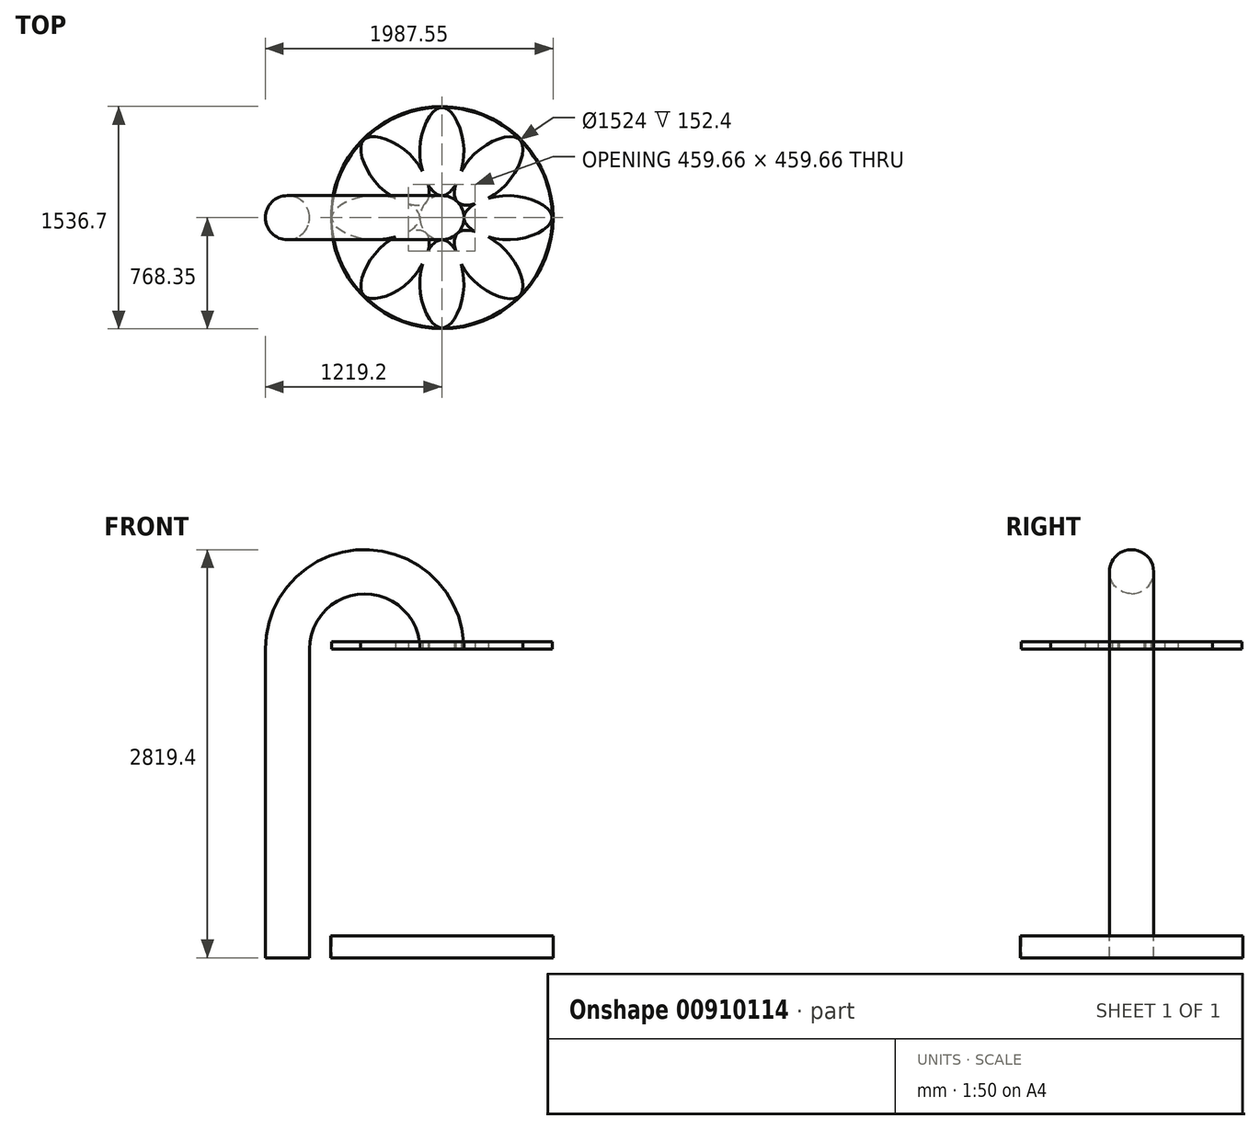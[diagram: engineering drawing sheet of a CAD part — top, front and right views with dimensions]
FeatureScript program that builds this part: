
annotation { "Feature Type Name" : "Feature", "Feature Type Description" : "" }
export const myFeature = defineFeature(function(context is Context, id is Id, definition is map)
    precondition{}
    {
        {
            var Q0;
            Q0=qCreatedBy(makeId("Top.planeOp"),FACE);
            var sketch = newSketch(context, id + "F0", { "sketchPlane" : qUnion([Q0])});
            skCircle(sketch, "E0", {"center": v(0, 0) * mm, "radius": 762 * mm});
            skCircle(sketch, "E1", {"center": v(0, 0) * mm, "radius": 768.35 * mm});
            skSolve(sketch);
        }
        {
            var Q0;
            Q0=qCreatedBy(makeId("Front.planeOp"),FACE);
            var sketch = newSketch(context, id + "F1", { "sketchPlane" : qUnion([Q0])});
            skLineSegment(sketch, "E2", {"start": v(-1066.8, 0) * mm, "end": v(-1066.8, 2133.6) * mm});
            skArc(sketch, "E3", {"start": v(0, 2133.6) * mm, "mid": v(-533.4, 2667) * mm, "end": v(-1066.8, 2133.6) * mm});
            skSolve(sketch);
        }
        {
            var Q0;
            Q0 = qSketchRegion(id + "F0", true);
            extrude(context, id + "F2", {"entities" : qUnion([Q0]), "depth" : 152.4 * mm, "offsetDistance" : 25.4 * mm});
        }
        {
            var Q0;
            Q0=qCreatedBy(makeId("Top.planeOp"),FACE);
            var sketch = newSketch(context, id + "F3", { "sketchPlane" : qUnion([Q0])});
            skCircle(sketch, "E4", {"center": v(-1066.8, 0) * mm, "radius": 152.4 * mm});
            skSolve(sketch);
        }
        {
            var Q0;
            Q0=makeQuery(id+"F3.imprint","IMPRINT",FACE,{"disambiguationData":[TD([[makeQuery(id+"F3.imprint","IMPRINT",EDGE,{"derivedFrom":sQuery(id+"F3.wireOp",EDGE,"E4")}),1.0]])]});
            var Q1;
            Q1=sQuery(id+"F1.wireOp",EDGE,"E2");
            var Q2;
            Q2=sQuery(id+"F1.wireOp",EDGE,"E3");
            sweep(context, id + "F4", {"profiles" : qUnion([Q0]), "path" : qUnion([Q1, Q2])});
        }
        {
            var Q0;
            Q0=makeQuery(id+"F4.opSweep","CAP_FACE",FACE,{"disambiguationData":[OSD([sQuery(id+"F1.wireOp",VERTEX,"E3.start"),sQuery(id+"F3.wireOp",EDGE,"E4")])],"isStart":false});
            var sketch = newSketch(context, id + "F5", { "sketchPlane" : qUnion([Q0])});
            skFitSpline(sketch, "E5", {"points": [v(0, 152.4) * mm, v(-152.4, 457.2) * mm, v(0, 762) * mm, v(152.4, 457.2) * mm, v(0, 152.4) * mm]});
            skPoint(sketch, "E6", {"position": v(152.4, 0) * mm});
            skPoint(sketch, "E7", {"position": v(-152.4, 0) * mm});
            skFitSpline(sketch, "E8", {"points": [v(152.4, 0) * mm, v(457.2, 152.4) * mm, v(762, 0) * mm, v(457.2, -152.4) * mm, v(152.4, 0) * mm]});
            skFitSpline(sketch, "E9", {"points": [v(0, -152.4) * mm, v(152.4, -457.2) * mm, v(0, -762) * mm, v(-152.4, -457.2) * mm, v(0, -152.4) * mm]});
            skFitSpline(sketch, "E10", {"points": [v(-762, 0) * mm, v(-457.2, 152.4) * mm, v(-152.4, 0) * mm, v(-457.2, -152.4) * mm, v(-762, 0) * mm]});
            skFitSpline(sketch, "E11", {"points": [v(-107.76, 107.76) * mm, v(-431.05, 215.53) * mm, v(-538.82, 538.82) * mm, v(-215.53, 431.05) * mm, v(-107.76, 107.76) * mm]});
            skFitSpline(sketch, "E12", {"points": [v(107.76, 107.76) * mm, v(215.53, 431.05) * mm, v(538.82, 538.82) * mm, v(431.05, 215.53) * mm, v(107.76, 107.76) * mm]});
            skFitSpline(sketch, "E13", {"points": [v(107.76, -107.76) * mm, v(431.05, -215.53) * mm, v(538.82, -538.82) * mm, v(215.53, -431.05) * mm, v(107.76, -107.76) * mm]});
            skFitSpline(sketch, "E14", {"points": [v(-538.82, -538.82) * mm, v(-431.05, -215.53) * mm, v(-107.76, -107.76) * mm, v(-215.53, -431.05) * mm, v(-538.82, -538.82) * mm]});
            skLineSegment(sketch, "E15", {"start": v(0, 0) * mm, "end": v(-107.76, -107.76) * mm});
            skSolve(sketch);
        }
        {
            var Q0;
            Q0 = qSketchRegion(id + "F5", true);
            extrude(context, id + "F6", {"entities" : qUnion([Q0]), "oppositeDirection" : true, "depth" : 50.8 * mm, "offsetDistance" : 25.4 * mm});
        }
    });
